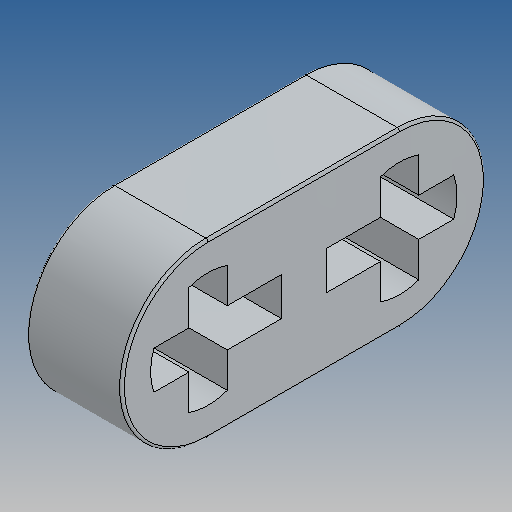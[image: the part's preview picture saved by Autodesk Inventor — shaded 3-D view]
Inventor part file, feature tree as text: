
AUTODESK INVENTOR PART (.ipt)
format: ipt  version: 2025 (Build 290162010, 162A)  size: 175,104 bytes
history: native  units: mm
features: extrude x1, fillet x1, sketch x1
ambient origin geometry x8: Origin, YZ Plane, XZ Plane, XY Plane, X Axis, Y Axis, Z Axis, Center Point
bodies: Solid1 (feature_tree)
feature tree (3):
  extrude  "Extrusion4"  Depth=7.2mm
  fillet  "Fillet1"  Radius=1.6mm
  sketch  "Sketch3"  dims[d15=4.0mm d16=0.0mm d47=4.8mm d49=7.2mm d53=1.6mm d56=0.1mm d57=0.8mm d58=8.0mm]
